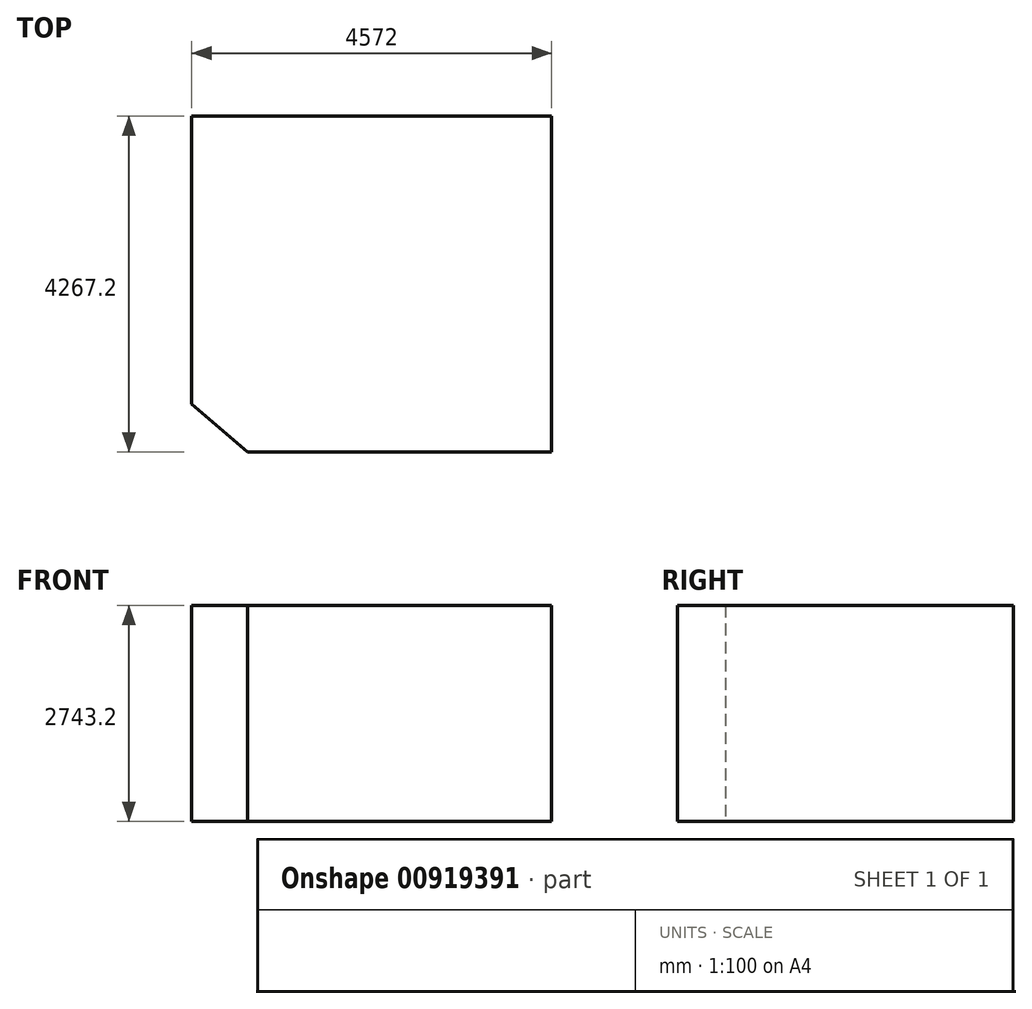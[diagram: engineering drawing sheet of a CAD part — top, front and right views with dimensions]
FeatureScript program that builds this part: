
annotation { "Feature Type Name" : "Feature", "Feature Type Description" : "" }
export const myFeature = defineFeature(function(context is Context, id is Id, definition is map)
    precondition{}
    {
        {
            var Q0;
            Q0=qCreatedBy(makeId("Top.planeOp"),FACE);
            var sketch = newSketch(context, id + "F0", { "sketchPlane" : qUnion([Q0])});
            skLineSegment(sketch, "E0.bottom", {"start": v(-2047.91, 2113.27) * mm, "end": v(2524.09, 2113.27) * mm});
            skLineSegment(sketch, "E0.top", {"start": v(-1340.38, -2153.93) * mm, "end": v(2524.09, -2153.93) * mm});
            skLineSegment(sketch, "E0.left", {"start": v(-2047.91, 2113.27) * mm, "end": v(-2047.91, -1544.33) * mm});
            skLineSegment(sketch, "E0.right", {"start": v(2524.09, 2113.27) * mm, "end": v(2524.09, -2153.93) * mm});
            skLineSegment(sketch, "E1", {"start": v(-571.54, -2153.93) * mm, "end": v(-571.54, -1849.13) * mm});
            skLineSegment(sketch, "E2", {"start": v(814.19, -2153.93) * mm, "end": v(814.19, -1849.13) * mm});
            skLineSegment(sketch, "E3", {"start": v(-2047.91, -1544.33) * mm, "end": v(-1340.38, -2153.93) * mm});
            skSolve(sketch);
        }
        {
            var Q0;
            Q0 = qSketchRegion(id + "F0", true);
            extrude(context, id + "F1", {"entities" : qUnion([Q0]), "depth" : 2743.2 * mm, "offsetDistance" : 30.48 * mm});
        }
    });
